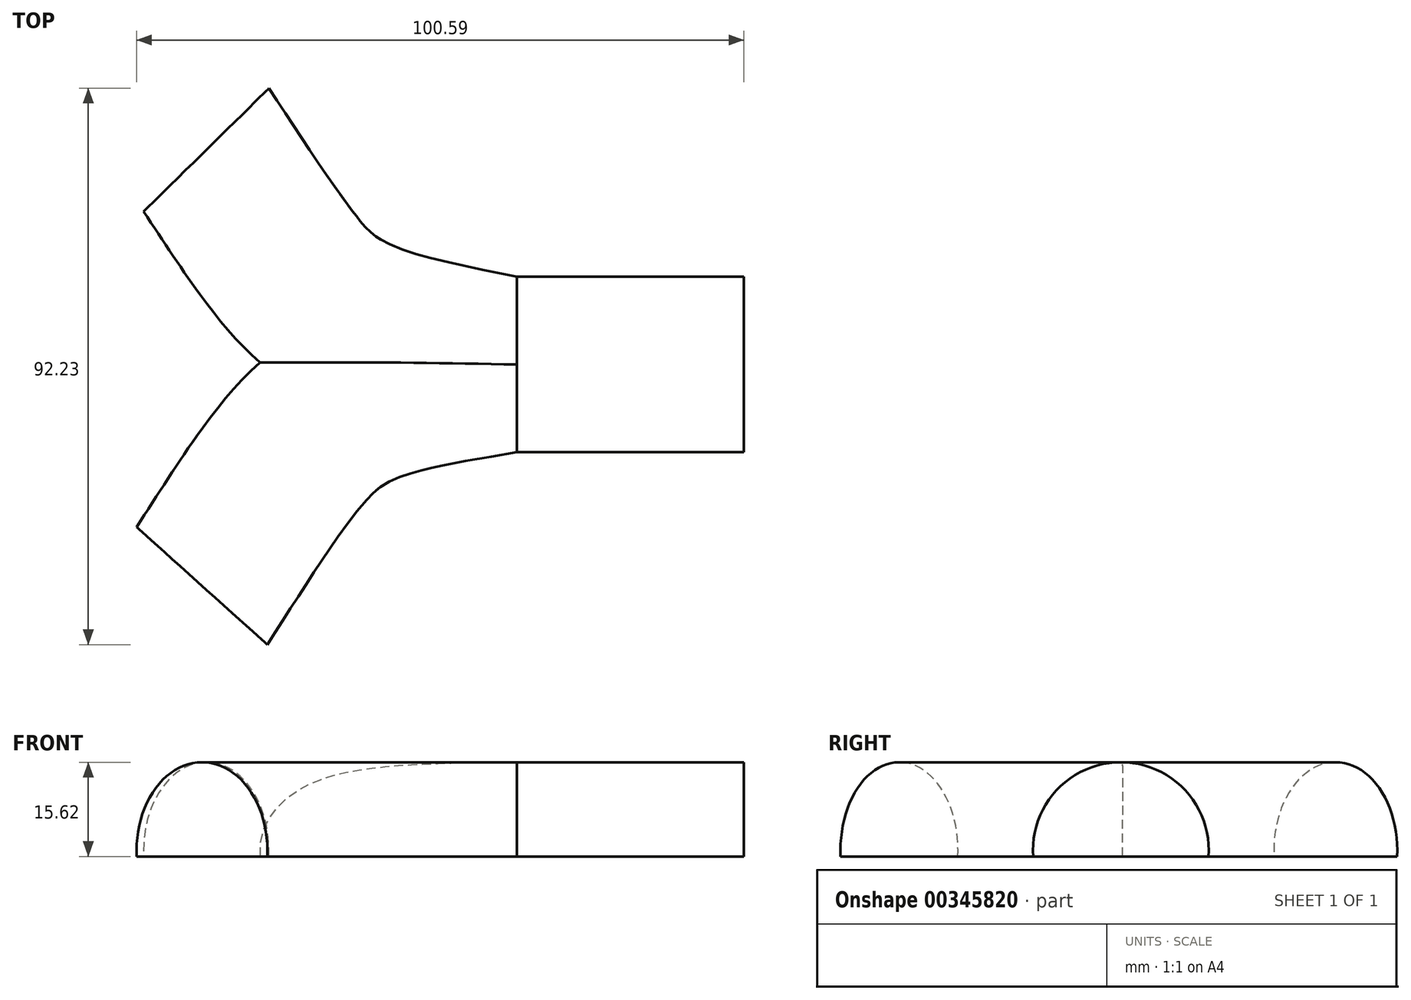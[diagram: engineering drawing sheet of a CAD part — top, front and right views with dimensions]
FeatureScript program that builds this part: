
annotation { "Feature Type Name" : "Feature", "Feature Type Description" : "" }
export const myFeature = defineFeature(function(context is Context, id is Id, definition is map)
    precondition{}
    {
        {
            var Q0;
            Q0=qCreatedBy(makeId("Top.planeOp"),FACE);
            var sketch = newSketch(context, id + "F0", { "sketchPlane" : qUnion([Q0])});
            skFitSpline(sketch, "E0", {"points": [v(0, 0) * mm, v(-51.8, 35.72) * mm], "startDerivative": vector(-97.75, 19.42) * mm, "endDerivative": vector(-57.65, 87.72) * mm});
            skFitSpline(sketch, "E1", {"points": [v(0, 0) * mm, v(-51.8, -36.55) * mm], "startDerivative": vector(-95.24, -15.67) * mm, "endDerivative": vector(-60.15, -94) * mm});
            skLineSegment(sketch, "E2", {"start": v(0, 0) * mm, "end": v(37.6, 0) * mm});
            skSolve(sketch);
        }
        {
            var Q0;
            Q0=qCreatedBy(makeId("Right.planeOp"),FACE);
            var sketch = newSketch(context, id + "F1", { "sketchPlane" : qUnion([Q0])});
            skLineSegment(sketch, "E3", {"start": v(0, -5.15) * mm, "end": v(-14.03, -5.15) * mm});
            skLineSegment(sketch, "E4", {"start": v(0, -5.15) * mm, "end": v(15, -5.15) * mm});
            skArc(sketch, "E5", {"start": v(15, -5.15) * mm, "mid": v(0.49, 10.47) * mm, "end": v(-14.03, -5.15) * mm});
            skSolve(sketch);
        }
        {
            var Q0;
            Q0=makeQuery(id+"F1.imprint","IMPRINT",FACE,{"disambiguationData":[TD([[makeQuery(id+"F1.imprint","IMPRINT",EDGE,{"derivedFrom":sQuery(id+"F1.wireOp",EDGE,"E3")}),-1.0]])]});
            var Q1;
            Q1=sQuery(id+"F0.wireOp",EDGE,"E0");
            sweep(context, id + "F2", {"profiles" : qUnion([Q0]), "path" : qUnion([Q1])});
        }
        {
            var Q0;
            Q0=makeQuery(id+"F2.opSweep","CAP_FACE",FACE,{"disambiguationData":[OSD([sQuery(id+"F0.wireOp",VERTEX,"E0.start"),sQuery(id+"F1.wireOp",EDGE,"E3"),sQuery(id+"F1.wireOp",EDGE,"E4"),sQuery(id+"F1.wireOp",EDGE,"E5")])],"isStart":true});
            var Q1;
            Q1=sQuery(id+"F0.wireOp",EDGE,"E1");
            sweep(context, id + "F3", {"operationType" : NewBodyOperationType.ADD, "profiles" : qUnion([Q0]), "path" : qUnion([Q1])});
        }
        {
            var Q0;
            Q0=makeQuery(id+"F2.opSweep","CAP_FACE",FACE,{"disambiguationData":[OSD([sQuery(id+"F0.wireOp",VERTEX,"E0.start"),sQuery(id+"F1.wireOp",EDGE,"E3"),sQuery(id+"F1.wireOp",EDGE,"E4"),sQuery(id+"F1.wireOp",EDGE,"E5")])],"isStart":true});
            var Q1;
            Q1=sQuery(id+"F0.wireOp",EDGE,"E2");
            sweep(context, id + "F4", {"operationType" : NewBodyOperationType.ADD, "profiles" : qUnion([Q0]), "path" : qUnion([Q1])});
        }
    });
